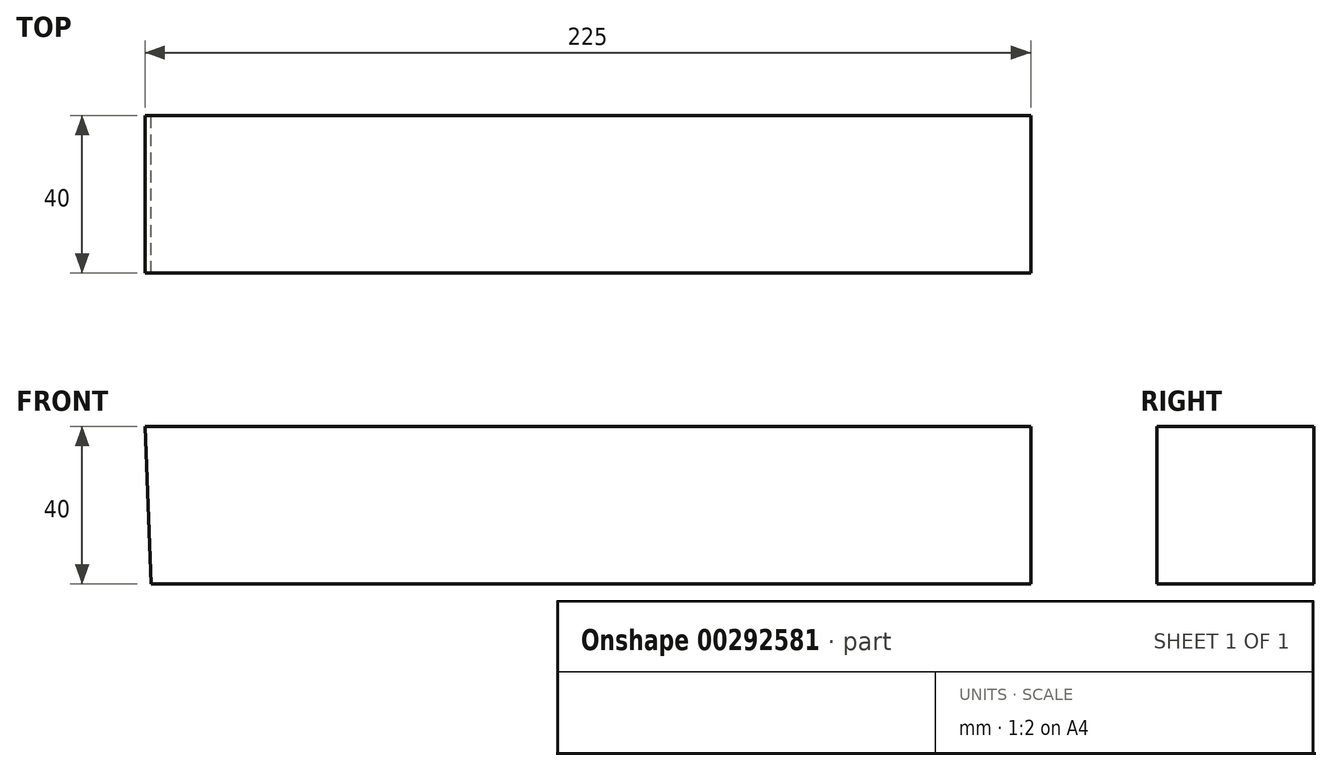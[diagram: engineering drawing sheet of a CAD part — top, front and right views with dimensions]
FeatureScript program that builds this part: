
annotation { "Feature Type Name" : "Feature", "Feature Type Description" : "" }
export const myFeature = defineFeature(function(context is Context, id is Id, definition is map)
    precondition{}
    {
        {
            var Q0;
            Q0=qCreatedBy(makeId("Front.planeOp"),FACE);
            var sketch = newSketch(context, id + "F0", { "sketchPlane" : qUnion([Q0])});
            skLineSegment(sketch, "E0", {"start": v(-110.4, -42.51) * mm, "end": v(114.6, -42.51) * mm});
            skLineSegment(sketch, "E1", {"start": v(114.6, -42.51) * mm, "end": v(114.6, -82.51) * mm});
            skLineSegment(sketch, "E2", {"start": v(114.6, -82.51) * mm, "end": v(-108.85, -82.51) * mm});
            skLineSegment(sketch, "E3", {"start": v(-108.85, -82.51) * mm, "end": v(-110.4, -42.51) * mm});
            skSolve(sketch);
        }
        {
            var Q0;
            Q0 = qSketchRegion(id + "F0", true);
            extrude(context, id + "F1", {"entities" : qUnion([Q0]), "depth" : 40 * mm});
        }
    });
